# Revit family: Motus Wall BL 800 940-927 CP1.4 D2W EU_Unhosted
name_source: partatom
category: Lighting Fixtures
revit_build: Autodesk Revit 2016 (Build: 20151007_0715(x64)
units: mm (PartAtom-declared; Revit-internal decimal feet)

## family parameters
Always vertical = Yes
Cut with Voids When Loaded = No
Light Source = Yes
OmniClass Number = 23.80.70.00
OmniClass Title = Lighting
Part Type = Normal
Room Calculation Point = No
Round Connector Dimension = Use Diameter
Shared = No
Work Plane-Based = No

## types (1)
- Motus Wall BL 800 940-927 CP1.4 D2W EU_Unhosted
    #Tubes = 1
    Apparent Load = 9 VA
    ArticleNumber = MOT028694
    Body Material and Colour = Default
    Color Filter = 16777215
    Description = Motus Wall BL 800 940-927 CP1.4 D2W EU
    Dimming Lamp Color Temperature Shift = <None>
    EANNo = 7040670286949
    Emit Shape Visible in Rendering = Yes
    Emit from Circle Diameter = 6 mm  [stored 0.019685 ft]
    Expired = 0
    Frequency = 50 Hz
    FrequencyMax = 60 Hz
    Glamox Category = Architectural
    Glamox Family = Motus Wall
    Glamox Mounting = Wall
    GlobalTradeItemNumber = 7040670286949
    Height = 98 mm
    IFC Classification = Light Fixture
    IPClass = 20
    IP_Code = 20
    Lamp = LED
    Lamp Wattage = 8 W
    Length = 98 mm
    LightFixtureMountingType = SURFACE
    LightFixturePlacingType = WALL
    MFArtNo = MOT028694
    MaintenanceFactor = 0
    Manufacturer = Glamox
    Maximum TA = 25
    ModelLabel = Motus Wall BL 800 940-927 CP1.4 D2W EU
    ModelReference = Motus Wall
    NominalFrequencyRange = 50 Hz
    Number of Poles = 1
    NumberOfSources = 1
    Optic = SYM
    Photometric Web File = MOTUS-WALL-800-D2W.ies
    Plug Type = EU
    Power Factor = 0.98
    PowerFactor = 98.00%
    RatedVoltage = 100 V
    Specification = colour Black, light source LED, with EU plug
    Tilt Angle = 90.00°
    Total Load = 8 W
    TotalWattage = 8 W
    TypeOfBallast = AC/DC = alternating current/ direct current
    URL Denmark = http://glamox.com
    URL Estonia = http://glamox.com
    URL Finland = http://glamox.com
    URL Germany = http://glamox.com
    URL Ireland = http://glamox.com
    URL Norway = http://glamox.com
    URL Other = http://glamox.com
    URL Russia = http://glamox.com
    URL Sweden = http://glamox.com
    URL UK = http://glamox.com
    UpdateDate = 20.02.2021 03:04:55
    Voltage = 100 V
    VoltageMax = 240 V
    Width = 165 mm

note: [stored X ft] marks values corroborated as IEEE doubles in the binary element streams (Revit-internal decimal feet)

## geometry (parser evidence)
native form markers: Blend x8, Sweep x1
no freeform markers — native parametric forms only
